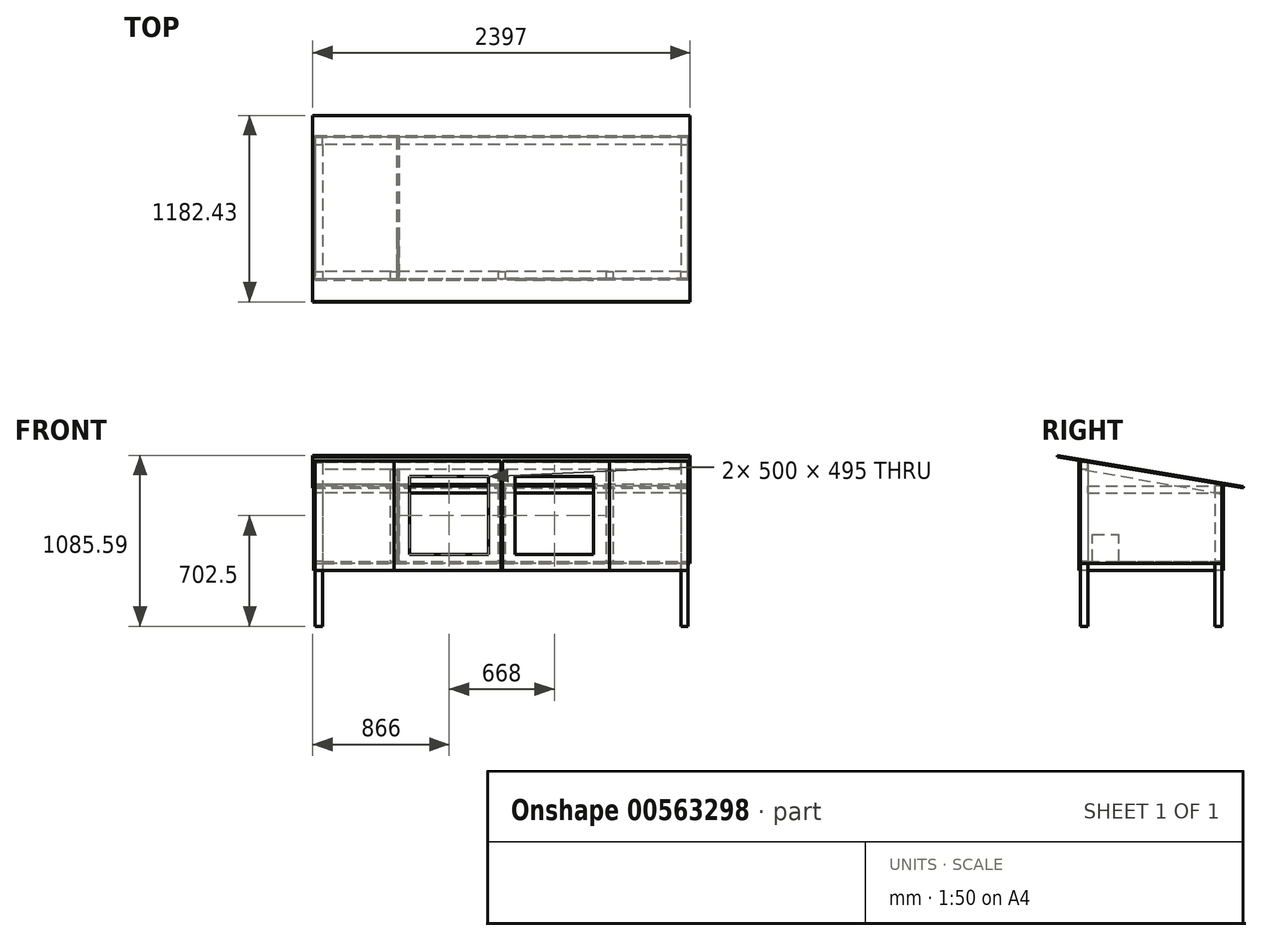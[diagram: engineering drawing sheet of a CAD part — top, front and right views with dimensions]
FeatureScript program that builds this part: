
annotation { "Feature Type Name" : "Feature", "Feature Type Description" : "" }
export const myFeature = defineFeature(function(context is Context, id is Id, definition is map)
    precondition{}
    {
        {
            var Q0;
            Q0=qCreatedBy(makeId("Top.planeOp"),FACE);
            var sketch = newSketch(context, id + "F0", { "sketchPlane" : qUnion([Q0])});
            skLineSegment(sketch, "E0.bottom", {"start": v(45, 0) * mm, "end": v(2323, 0) * mm});
            skLineSegment(sketch, "E0.top", {"start": v(45, 897) * mm, "end": v(2323, 897) * mm});
            skLineSegment(sketch, "E0.left", {"start": v(0, 45) * mm, "end": v(0, 852) * mm});
            skLineSegment(sketch, "E0.right", {"start": v(2368, 45) * mm, "end": v(2368, 852) * mm});
            skLineSegment(sketch, "E1", {"start": v(0, 45) * mm, "end": v(45, 45) * mm});
            skLineSegment(sketch, "E2", {"start": v(45, 45) * mm, "end": v(45, 0) * mm});
            skLineSegment(sketch, "E3", {"start": v(45, 897) * mm, "end": v(45, 852) * mm});
            skLineSegment(sketch, "E4", {"start": v(45, 852) * mm, "end": v(0, 852) * mm});
            skLineSegment(sketch, "E5", {"start": v(2323, 897) * mm, "end": v(2323, 852) * mm});
            skLineSegment(sketch, "E6", {"start": v(2323, 852) * mm, "end": v(2368, 852) * mm});
            skLineSegment(sketch, "E7", {"start": v(2323, 0) * mm, "end": v(2323, 45) * mm});
            skLineSegment(sketch, "E8", {"start": v(2323, 45) * mm, "end": v(2368, 45) * mm});
            skPoint(sketch, "E9.orphan", {"position": v(2368, 897) * mm});
            skSolve(sketch);
        }
        {
            var Q0;
            Q0 = qSketchRegion(id + "F0", true);
            extrude(context, id + "F1", {"entities" : qUnion([Q0]), "depth" : 11 * mm, "offsetDistance" : 25 * mm});
        }
        {
            var Q0;
            Q0=qCreatedBy(makeId("Right.planeOp"),FACE);
            var sketch = newSketch(context, id + "F2", { "sketchPlane" : qUnion([Q0])});
            skLineSegment(sketch, "E10", {"start": v(897, 0) * mm, "end": v(897, 500) * mm});
            skLineSegment(sketch, "E11", {"start": v(897, 500) * mm, "end": v(0, 650) * mm});
            skLineSegment(sketch, "E12", {"start": v(0, 650) * mm, "end": v(0, 0) * mm});
            skLineSegment(sketch, "E13", {"start": v(0, 0) * mm, "end": v(0, -45) * mm});
            skLineSegment(sketch, "E14", {"start": v(0, -45) * mm, "end": v(897, -45) * mm});
            skLineSegment(sketch, "E15", {"start": v(897, -45) * mm, "end": v(897, 0) * mm});
            skSolve(sketch);
        }
        {
            var Q0;
            Q0 = qSketchRegion(id + "F2", true);
            extrude(context, id + "F3", {"entities" : qUnion([Q0]), "oppositeDirection" : true, "depth" : 11 * mm, "offsetDistance" : 25 * mm});
        }
        {
            var Q0;
            Q0=makeQuery(id+"F1.opExtrude","SWEPT_FACE",FACE,{"disambiguationData":[OSD([sQuery(id+"F0.wireOp",EDGE,"E0.right")])]});
            var sketch = newSketch(context, id + "F4", { "sketchPlane" : qUnion([Q0])});
            skLineSegment(sketch, "E16", {"start": v(0, 0) * mm, "end": v(897, 0) * mm});
            skLineSegment(sketch, "E17", {"start": v(897, 0) * mm, "end": v(897, 500) * mm});
            skLineSegment(sketch, "E18", {"start": v(897, 500) * mm, "end": v(0, 650) * mm});
            skLineSegment(sketch, "E19", {"start": v(0, 650) * mm, "end": v(0, 0) * mm});
            skSolve(sketch);
        }
        {
            var Q0;
            Q0 = qSketchRegion(id + "F4", true);
            extrude(context, id + "F5", {"entities" : qUnion([Q0]), "depth" : 11 * mm, "offsetDistance" : 25 * mm});
        }
        {
            var Q0;
            Q0=makeQuery(id+"F1.opExtrude","SWEPT_FACE",FACE,{"disambiguationData":[OSD([sQuery(id+"F0.wireOp",EDGE,"E0.top")])]});
            var sketch = newSketch(context, id + "F6", { "sketchPlane" : qUnion([Q0])});
            skLineSegment(sketch, "E20", {"start": v(0, -45) * mm, "end": v(-2368, -45) * mm});
            skLineSegment(sketch, "E21", {"start": v(-2368, -45) * mm, "end": v(-2368, 500) * mm});
            skLineSegment(sketch, "E22", {"start": v(-2368, 500) * mm, "end": v(0, 500) * mm});
            skLineSegment(sketch, "E23", {"start": v(0, 500) * mm, "end": v(0, -45) * mm});
            skSolve(sketch);
        }
        {
            var Q0;
            Q0 = qSketchRegion(id + "F6", true);
            extrude(context, id + "F7", {"entities" : qUnion([Q0]), "depth" : 11 * mm, "offsetDistance" : 25 * mm});
        }
        {
            var Q0;
            Q0=makeQuery(id+"F3.opExtrude","SWEPT_FACE",FACE,{"disambiguationData":[OSD([sQuery(id+"F2.wireOp",EDGE,"E11")])]});
            var sketch = newSketch(context, id + "F8", { "sketchPlane" : qUnion([Q0])});
            skLineSegment(sketch, "E24.bottom", {"start": v(-16, -257.2) * mm, "end": v(2381, -257.2) * mm});
            skLineSegment(sketch, "E24.top", {"start": v(-16, 939.8) * mm, "end": v(2381, 939.8) * mm});
            skLineSegment(sketch, "E24.left", {"start": v(-16, -257.2) * mm, "end": v(-16, 939.8) * mm});
            skLineSegment(sketch, "E24.right", {"start": v(2381, -257.2) * mm, "end": v(2381, 939.8) * mm});
            skSolve(sketch);
        }
        {
            var Q0;
            Q0 = qSketchRegion(id + "F8", true);
            extrude(context, id + "F9", {"entities" : qUnion([Q0]), "depth" : 11 * mm, "offsetDistance" : 25 * mm});
        }
        {
            var Q0;
            Q0=qCreatedBy(makeId("Front.planeOp"),FACE);
            var sketch = newSketch(context, id + "F10", { "sketchPlane" : qUnion([Q0])});
            skLineSegment(sketch, "E25.bottom", {"start": v(0, -45) * mm, "end": v(500, -45) * mm});
            skLineSegment(sketch, "E25.top", {"start": v(0, 650) * mm, "end": v(500, 650) * mm});
            skLineSegment(sketch, "E25.left", {"start": v(0, -45) * mm, "end": v(0, 650) * mm});
            skLineSegment(sketch, "E25.right", {"start": v(500, -45) * mm, "end": v(500, 650) * mm});
            skLineSegment(sketch, "E26.bottom", {"start": v(2368, -45) * mm, "end": v(1868, -45) * mm});
            skLineSegment(sketch, "E26.top", {"start": v(2368, 650) * mm, "end": v(1868, 650) * mm});
            skLineSegment(sketch, "E26.left", {"start": v(2368, -45) * mm, "end": v(2368, 650) * mm});
            skLineSegment(sketch, "E26.right", {"start": v(1868, -45) * mm, "end": v(1868, 650) * mm});
            skSolve(sketch);
        }
        {
            var Q0;
            Q0 = qSketchRegion(id + "F10", true);
            extrude(context, id + "F11", {"entities" : qUnion([Q0]), "depth" : 11 * mm, "offsetDistance" : 25 * mm});
        }
        {
            var Q0;
            Q0=qCreatedBy(makeId("Top.planeOp"),FACE);
            var sketch = newSketch(context, id + "F12", { "sketchPlane" : qUnion([Q0])});
            skLineSegment(sketch, "E27.bottom", {"start": v(0, 0) * mm, "end": v(45, 0) * mm});
            skLineSegment(sketch, "E27.top", {"start": v(0, 45) * mm, "end": v(45, 45) * mm});
            skLineSegment(sketch, "E27.left", {"start": v(0, 0) * mm, "end": v(0, 45) * mm});
            skLineSegment(sketch, "E27.right", {"start": v(45, 0) * mm, "end": v(45, 45) * mm});
            skLineSegment(sketch, "E28.bottom", {"start": v(2368, 0) * mm, "end": v(2323, 0) * mm});
            skLineSegment(sketch, "E28.top", {"start": v(2368, 45) * mm, "end": v(2323, 45) * mm});
            skLineSegment(sketch, "E28.left", {"start": v(2368, 0) * mm, "end": v(2368, 45) * mm});
            skLineSegment(sketch, "E28.right", {"start": v(2323, 0) * mm, "end": v(2323, 45) * mm});
            skSolve(sketch);
        }
        {
            var Q0;
            Q0 = qSketchRegion(id + "F12", true);
            extrude(context, id + "F13", {"entities" : qUnion([Q0]), "depth" : 640 * mm, "offsetDistance" : 25 * mm, "hasSecondDirection" : true, "secondDirectionOppositeDirection" : true, "secondDirectionDepth" : 400 * mm});
        }
        {
            var Q0;
            Q0=qCreatedBy(makeId("Front.planeOp"),FACE);
            var sketch = newSketch(context, id + "F14", { "sketchPlane" : qUnion([Q0])});
            skLineSegment(sketch, "E29.bottom", {"start": v(500, -45) * mm, "end": v(1180, -45) * mm});
            skLineSegment(sketch, "E29.top", {"start": v(500, 650) * mm, "end": v(1180, 650) * mm});
            skLineSegment(sketch, "E29.left", {"start": v(500, -45) * mm, "end": v(500, 650) * mm});
            skLineSegment(sketch, "E29.right", {"start": v(1180, -45) * mm, "end": v(1180, 650) * mm});
            skPoint(sketch, "E30.firstSnap0", {"position": v(840, -45) * mm});
            skLineSegment(sketch, "E30.bottom", {"start": v(1868, -45) * mm, "end": v(1188, -45) * mm});
            skLineSegment(sketch, "E30.top", {"start": v(1868, 650) * mm, "end": v(1188, 650) * mm});
            skLineSegment(sketch, "E30.left", {"start": v(1868, -45) * mm, "end": v(1868, 650) * mm});
            skLineSegment(sketch, "E30.right", {"start": v(1188, -45) * mm, "end": v(1188, 650) * mm});
            skLineSegment(sketch, "E31.bottom", {"start": v(600, 550) * mm, "end": v(1100, 550) * mm});
            skLineSegment(sketch, "E31.top", {"start": v(600, 55) * mm, "end": v(1100, 55) * mm});
            skLineSegment(sketch, "E31.left", {"start": v(600, 550) * mm, "end": v(600, 55) * mm});
            skLineSegment(sketch, "E31.right", {"start": v(1100, 550) * mm, "end": v(1100, 55) * mm});
            skLineSegment(sketch, "E32.bottom", {"start": v(1268, 550) * mm, "end": v(1768, 550) * mm});
            skLineSegment(sketch, "E32.top", {"start": v(1268, 55) * mm, "end": v(1768, 55) * mm});
            skLineSegment(sketch, "E32.left", {"start": v(1268, 550) * mm, "end": v(1268, 55) * mm});
            skLineSegment(sketch, "E32.right", {"start": v(1768, 550) * mm, "end": v(1768, 55) * mm});
            skSolve(sketch);
        }
        {
            var Q0;
            Q0 = qSketchRegion(id + "F14", true);
            extrude(context, id + "F15", {"entities" : qUnion([Q0]), "depth" : 11 * mm, "offsetDistance" : 25 * mm});
        }
        {
            var Q0;
            Q0=qCreatedBy(makeId("Top.planeOp"),FACE);
            var sketch = newSketch(context, id + "F16", { "sketchPlane" : qUnion([Q0])});
            skLineSegment(sketch, "E33.bottom", {"start": v(0, 852) * mm, "end": v(45, 852) * mm});
            skLineSegment(sketch, "E33.top", {"start": v(0, 897) * mm, "end": v(45, 897) * mm});
            skLineSegment(sketch, "E33.left", {"start": v(0, 852) * mm, "end": v(0, 897) * mm});
            skLineSegment(sketch, "E33.right", {"start": v(45, 852) * mm, "end": v(45, 897) * mm});
            skLineSegment(sketch, "E34.bottom", {"start": v(2323, 852) * mm, "end": v(2368, 852) * mm});
            skLineSegment(sketch, "E34.top", {"start": v(2323, 897) * mm, "end": v(2368, 897) * mm});
            skLineSegment(sketch, "E34.left", {"start": v(2323, 852) * mm, "end": v(2323, 897) * mm});
            skLineSegment(sketch, "E34.right", {"start": v(2368, 852) * mm, "end": v(2368, 897) * mm});
            skSolve(sketch);
        }
        {
            var Q0;
            Q0 = qSketchRegion(id + "F16", true);
            extrude(context, id + "F17", {"entities" : qUnion([Q0]), "depth" : 490 * mm, "offsetDistance" : 25 * mm, "hasSecondDirection" : true, "secondDirectionOppositeDirection" : true, "secondDirectionDepth" : 400 * mm});
        }
        {
            var Q0;
            Q0=makeQuery(id+"F13.opExtrude","SWEPT_FACE",FACE,{"disambiguationData":[OSD([sQuery(id+"F12.wireOp",EDGE,"E27.top")])]});
            var sketch = newSketch(context, id + "F18", { "sketchPlane" : qUnion([Q0])});
            skLineSegment(sketch, "E35.bottom", {"start": v(0, 0) * mm, "end": v(-45, 0) * mm});
            skLineSegment(sketch, "E35.top", {"start": v(0, -45) * mm, "end": v(-45, -45) * mm});
            skLineSegment(sketch, "E35.left", {"start": v(0, 0) * mm, "end": v(0, -45) * mm});
            skLineSegment(sketch, "E35.right", {"start": v(-45, 0) * mm, "end": v(-45, -45) * mm});
            skSolve(sketch);
        }
        {
            var Q0;
            Q0 = qSketchRegion(id + "F18", true);
            extrude(context, id + "F19", {"entities" : qUnion([Q0]), "endBound" : BoundingType.UP_TO_NEXT, "depth" : 25 * mm, "offsetDistance" : 25 * mm});
        }
        {
            var Q0;
            Q0=makeQuery(id+"F13.opExtrude","SWEPT_FACE",FACE,{"disambiguationData":[OSD([sQuery(id+"F12.wireOp",EDGE,"E28.top")])]});
            var sketch = newSketch(context, id + "F20", { "sketchPlane" : qUnion([Q0])});
            skLineSegment(sketch, "E36.bottom", {"start": v(-2368, 0) * mm, "end": v(-2323, 0) * mm});
            skLineSegment(sketch, "E36.top", {"start": v(-2368, -45) * mm, "end": v(-2323, -45) * mm});
            skLineSegment(sketch, "E36.left", {"start": v(-2368, 0) * mm, "end": v(-2368, -45) * mm});
            skLineSegment(sketch, "E36.right", {"start": v(-2323, 0) * mm, "end": v(-2323, -45) * mm});
            skSolve(sketch);
        }
        {
            var Q0;
            Q0 = qSketchRegion(id + "F20", true);
            extrude(context, id + "F21", {"entities" : qUnion([Q0]), "endBound" : BoundingType.UP_TO_NEXT, "depth" : 25 * mm, "offsetDistance" : 25 * mm});
        }
        {
            var Q0;
            Q0=makeQuery(id+"F13.opExtrude","SWEPT_FACE",FACE,{"disambiguationData":[OSD([sQuery(id+"F12.wireOp",EDGE,"E27.right")])]});
            var sketch = newSketch(context, id + "F22", { "sketchPlane" : qUnion([Q0])});
            skLineSegment(sketch, "E37.bottom", {"start": v(0, 0) * mm, "end": v(45, 0) * mm});
            skLineSegment(sketch, "E37.top", {"start": v(0, -45) * mm, "end": v(45, -45) * mm});
            skLineSegment(sketch, "E37.left", {"start": v(0, 0) * mm, "end": v(0, -45) * mm});
            skLineSegment(sketch, "E37.right", {"start": v(45, 0) * mm, "end": v(45, -45) * mm});
            skLineSegment(sketch, "E38.bottom", {"start": v(852, 0) * mm, "end": v(897, 0) * mm});
            skLineSegment(sketch, "E38.top", {"start": v(852, -45) * mm, "end": v(897, -45) * mm});
            skLineSegment(sketch, "E38.left", {"start": v(852, 0) * mm, "end": v(852, -45) * mm});
            skLineSegment(sketch, "E38.right", {"start": v(897, 0) * mm, "end": v(897, -45) * mm});
            skSolve(sketch);
        }
        {
            var Q0;
            Q0 = qSketchRegion(id + "F22", true);
            extrude(context, id + "F23", {"entities" : qUnion([Q0]), "endBound" : BoundingType.UP_TO_NEXT, "depth" : 25 * mm, "offsetDistance" : 25 * mm});
        }
        {
            var Q0;
            Q0=makeQuery(id+"F13.opExtrude","SWEPT_FACE",FACE,{"disambiguationData":[OSD([sQuery(id+"F12.wireOp",EDGE,"E27.right")])]});
            var sketch = newSketch(context, id + "F24", { "sketchPlane" : qUnion([Q0])});
            skLineSegment(sketch, "E39.bottom", {"start": v(0, 640) * mm, "end": v(45, 640) * mm});
            skLineSegment(sketch, "E39.top", {"start": v(0, 595) * mm, "end": v(45, 595) * mm});
            skLineSegment(sketch, "E39.left", {"start": v(0, 640) * mm, "end": v(0, 595) * mm});
            skLineSegment(sketch, "E39.right", {"start": v(45, 640) * mm, "end": v(45, 595) * mm});
            skLineSegment(sketch, "E40.bottom", {"start": v(852, 490) * mm, "end": v(897, 490) * mm});
            skLineSegment(sketch, "E40.top", {"start": v(852, 445) * mm, "end": v(897, 445) * mm});
            skLineSegment(sketch, "E40.left", {"start": v(852, 490) * mm, "end": v(852, 445) * mm});
            skLineSegment(sketch, "E40.right", {"start": v(897, 490) * mm, "end": v(897, 445) * mm});
            skSolve(sketch);
        }
        {
            var Q0;
            Q0 = qSketchRegion(id + "F24", true);
            extrude(context, id + "F25", {"entities" : qUnion([Q0]), "endBound" : BoundingType.UP_TO_NEXT, "depth" : 25 * mm, "offsetDistance" : 25 * mm});
        }
        {
            var Q0;
            Q0=makeQuery(id+"F17.opExtrude","SWEPT_FACE",FACE,{"disambiguationData":[OSD([sQuery(id+"F16.wireOp",EDGE,"E33.bottom")])]});
            var sketch = newSketch(context, id + "F26", { "sketchPlane" : qUnion([Q0])});
            skLineSegment(sketch, "E41.bottom", {"start": v(0, 490) * mm, "end": v(45, 490) * mm});
            skLineSegment(sketch, "E41.top", {"start": v(0, 445) * mm, "end": v(45, 445) * mm});
            skLineSegment(sketch, "E41.left", {"start": v(0, 490) * mm, "end": v(0, 445) * mm});
            skLineSegment(sketch, "E41.right", {"start": v(45, 490) * mm, "end": v(45, 445) * mm});
            skLineSegment(sketch, "E42.bottom", {"start": v(2323, 490) * mm, "end": v(2368, 490) * mm});
            skLineSegment(sketch, "E42.top", {"start": v(2323, 445) * mm, "end": v(2368, 445) * mm});
            skLineSegment(sketch, "E42.left", {"start": v(2323, 490) * mm, "end": v(2323, 445) * mm});
            skLineSegment(sketch, "E42.right", {"start": v(2368, 490) * mm, "end": v(2368, 445) * mm});
            skSolve(sketch);
        }
        {
            var Q0;
            Q0 = qSketchRegion(id + "F26", true);
            extrude(context, id + "F27", {"entities" : qUnion([Q0]), "endBound" : BoundingType.UP_TO_NEXT, "depth" : 25 * mm, "offsetDistance" : 25 * mm});
        }
        {
            var Q0;
            Q0=makeQuery(id+"F1.opExtrude","CAP_FACE",FACE,{"disambiguationData":[OSD([sQuery(id+"F0.wireOp",EDGE,"E0.bottom"),sQuery(id+"F0.wireOp",EDGE,"E0.top"),sQuery(id+"F0.wireOp",EDGE,"E0.left"),sQuery(id+"F0.wireOp",EDGE,"E0.right"),sQuery(id+"F0.wireOp",EDGE,"E1"),sQuery(id+"F0.wireOp",EDGE,"E2"),sQuery(id+"F0.wireOp",EDGE,"E3"),sQuery(id+"F0.wireOp",EDGE,"E4"),sQuery(id+"F0.wireOp",EDGE,"E5"),sQuery(id+"F0.wireOp",EDGE,"E6"),sQuery(id+"F0.wireOp",EDGE,"E7"),sQuery(id+"F0.wireOp",EDGE,"E8")])],"isStart":false});
            var sketch = newSketch(context, id + "F28", { "sketchPlane" : qUnion([Q0])});
            skLineSegment(sketch, "E43.bottom", {"start": v(1160, 45) * mm, "end": v(1205, 45) * mm});
            skLineSegment(sketch, "E43.top", {"start": v(1160, 0) * mm, "end": v(1205, 0) * mm});
            skLineSegment(sketch, "E43.left", {"start": v(1160, 45) * mm, "end": v(1160, 0) * mm});
            skLineSegment(sketch, "E43.right", {"start": v(1205, 45) * mm, "end": v(1205, 0) * mm});
            skLineSegment(sketch, "E44.bottom", {"start": v(1845, 45) * mm, "end": v(1890, 45) * mm});
            skLineSegment(sketch, "E44.top", {"start": v(1845, 0) * mm, "end": v(1890, 0) * mm});
            skLineSegment(sketch, "E44.left", {"start": v(1845, 45) * mm, "end": v(1845, 0) * mm});
            skLineSegment(sketch, "E44.right", {"start": v(1890, 45) * mm, "end": v(1890, 0) * mm});
            skPoint(sketch, "E45.firstSnap0", {"position": v(1867.5, 45) * mm});
            skLineSegment(sketch, "E45.bottom", {"start": v(475, 45) * mm, "end": v(520, 45) * mm});
            skLineSegment(sketch, "E45.top", {"start": v(475, 0) * mm, "end": v(520, 0) * mm});
            skLineSegment(sketch, "E45.left", {"start": v(475, 45) * mm, "end": v(475, 0) * mm});
            skLineSegment(sketch, "E45.right", {"start": v(520, 45) * mm, "end": v(520, 0) * mm});
            skSolve(sketch);
        }
        {
            var Q0;
            Q0 = qSketchRegion(id + "F28", true);
            extrude(context, id + "F29", {"entities" : qUnion([Q0]), "endBound" : BoundingType.UP_TO_NEXT, "depth" : 25 * mm, "offsetDistance" : 25 * mm});
        }
        {
            var Q0;
            Q0=makeQuery(id+"F29.opExtrude","SWEPT_FACE",FACE,{"disambiguationData":[OSD([sQuery(id+"F28.wireOp",EDGE,"E45.right")])]});
            var sketch = newSketch(context, id + "F30", { "sketchPlane" : qUnion([Q0])});
            skLineSegment(sketch, "E46", {"start": v(0, 11) * mm, "end": v(76.04, 11) * mm});
            skLineSegment(sketch, "E47", {"start": v(897, 11) * mm, "end": v(897, 437.63) * mm});
            skLineSegment(sketch, "E48", {"start": v(897, 437.63) * mm, "end": v(0, 595) * mm});
            skLineSegment(sketch, "E49", {"start": v(0, 595) * mm, "end": v(0, 11) * mm});
            skLineSegment(sketch, "E50.top", {"start": v(76.04, 184.03) * mm, "end": v(244.59, 184.03) * mm});
            skLineSegment(sketch, "E50.left", {"start": v(76.04, 11) * mm, "end": v(76.04, 184.03) * mm});
            skLineSegment(sketch, "E50.right", {"start": v(244.59, 11) * mm, "end": v(244.59, 184.03) * mm});
            skLineSegment(sketch, "E51.trimOffspring", {"start": v(244.59, 11) * mm, "end": v(897, 11) * mm});
            skSolve(sketch);
        }
        {
            var Q0;
            Q0 = qSketchRegion(id + "F30", true);
            extrude(context, id + "F31", {"entities" : qUnion([Q0]), "depth" : 11 * mm, "offsetDistance" : 25 * mm});
        }
    });
